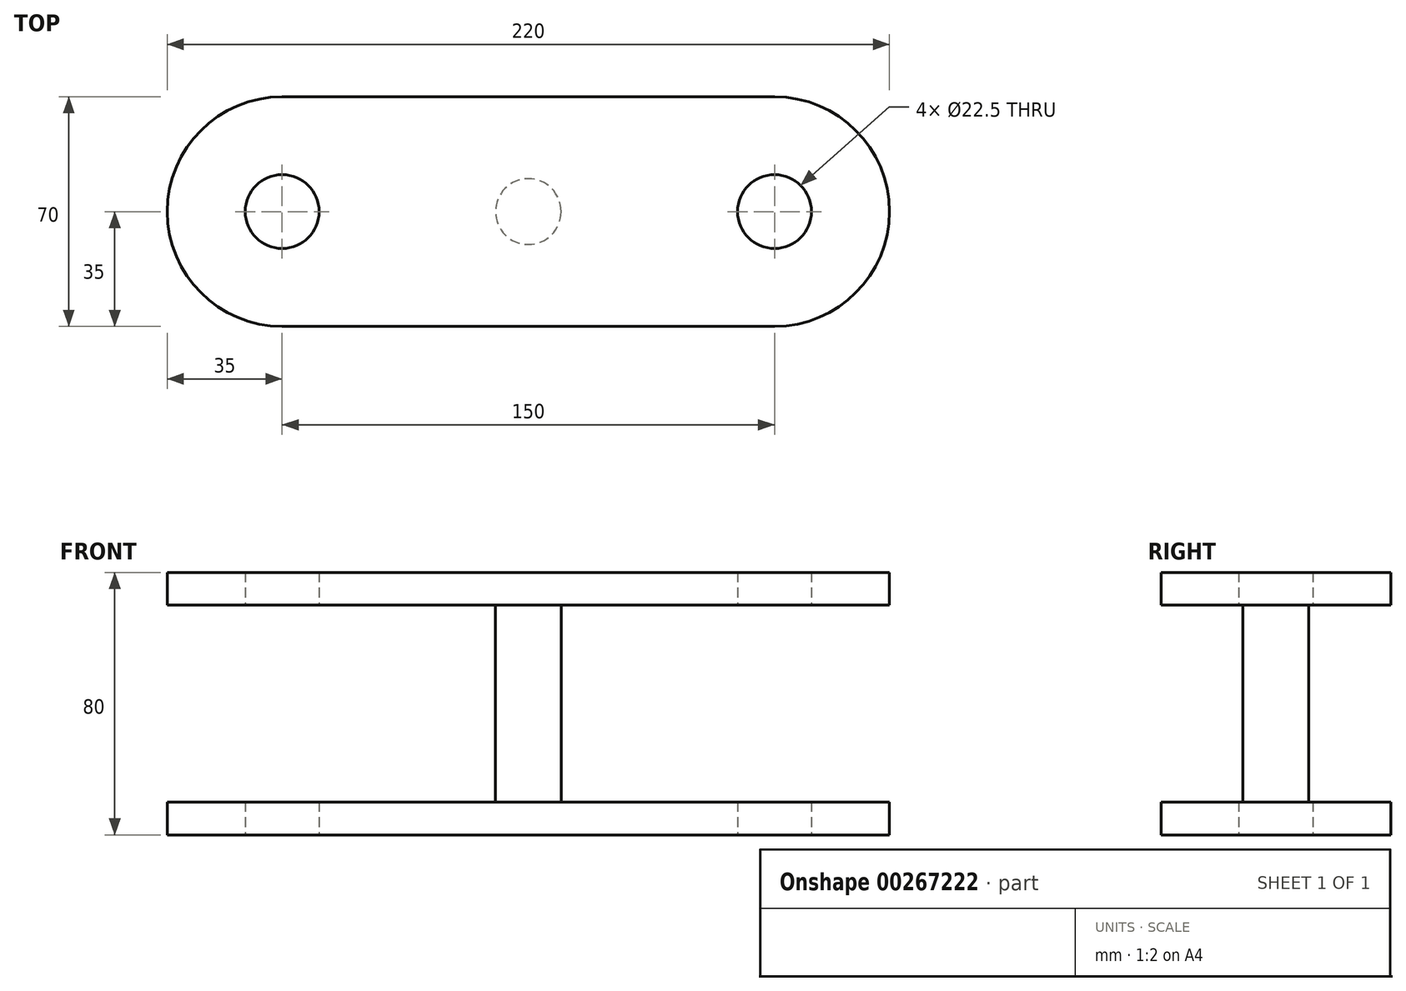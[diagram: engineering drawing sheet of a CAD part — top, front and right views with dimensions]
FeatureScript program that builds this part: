
annotation { "Feature Type Name" : "Feature", "Feature Type Description" : "" }
export const myFeature = defineFeature(function(context is Context, id is Id, definition is map)
    precondition{}
    {
        {
            var Q0;
            Q0=qCreatedBy(makeId("Top.planeOp"),FACE);
            var sketch = newSketch(context, id + "F0", { "sketchPlane" : qUnion([Q0])});
            skArc(sketch, "E0", {"start": v(-75, 35) * mm, "mid": v(-110, 0) * mm, "end": v(-75, -35) * mm});
            skArc(sketch, "E1", {"start": v(75, -35) * mm, "mid": v(110, 0) * mm, "end": v(75, 35) * mm});
            skLineSegment(sketch, "E2", {"start": v(-75, 35) * mm, "end": v(75, 35) * mm});
            skLineSegment(sketch, "E3", {"start": v(-75, -35) * mm, "end": v(75, -35) * mm});
            skArc(sketch, "E4", {"start": v(42.5, 0) * mm, "mid": v(75, -32.5) * mm, "end": v(107.5, 0) * mm});
            skArc(sketch, "E5", {"start": v(-107.5, 0) * mm, "mid": v(-75, -32.5) * mm, "end": v(-42.5, 0) * mm});
            skLineSegment(sketch, "E6", {"start": v(-42.5, 0) * mm, "end": v(-107.5, 0) * mm});
            skLineSegment(sketch, "E7", {"start": v(42.5, 0) * mm, "end": v(107.5, 0) * mm});
            skCircle(sketch, "E8", {"center": v(-75, 0) * mm, "radius": 11.25 * mm});
            skCircle(sketch, "E9", {"center": v(75, 0) * mm, "radius": 11.25 * mm});
            skCircle(sketch, "E10", {"center": v(0, 0) * mm, "radius": 10 * mm});
            skSolve(sketch);
        }
        {
            var Q0;
            {var subQ0=sQuery(id+"F0.wireOp",EDGE,"E5");Q0=makeQuery(id+"F0.imprint","IMPRINT",FACE,{"disambiguationData":[TD([[makeQuery(id+"F0.imprint","IMPRINT",EDGE,{"derivedFrom":subQ0}),1.0]])]});}
            var Q1;
            {var subQ0=sQuery(id+"F0.wireOp",EDGE,"E4");Q1=makeQuery(id+"F0.imprint","IMPRINT",FACE,{"disambiguationData":[TD([[makeQuery(id+"F0.imprint","IMPRINT",EDGE,{"derivedFrom":subQ0}),1.0]])]});}
            var Q2;
            Q2=makeQuery(id+"F0.imprint","IMPRINT",FACE,{"disambiguationData":[TD([[makeQuery(id+"F0.imprint","IMPRINT",EDGE,{"derivedFrom":sQuery(id+"F0.wireOp",EDGE,"E0")}),1.0]])]});
            var Q3;
            Q3=makeQuery(id+"F0.imprint","IMPRINT",FACE,{"disambiguationData":[TD([[makeQuery(id+"F0.imprint","IMPRINT",EDGE,{"derivedFrom":sQuery(id+"F0.wireOp",EDGE,"E10")}),1.0]])]});
            extrude(context, id + "F1", {"entities" : qUnion([Q0, Q1, Q2, Q3]), "endBound" : BoundingType.SYMMETRIC, "depth" : 80 * mm});
        }
        {
            var Q0;
            Q0=makeQuery(id+"F0.imprint","IMPRINT",FACE,{"disambiguationData":[TD([[makeQuery(id+"F0.imprint","IMPRINT",EDGE,{"derivedFrom":sQuery(id+"F0.wireOp",EDGE,"E5")}),1.0]])]});
            var Q1;
            Q1=makeQuery(id+"F0.imprint","IMPRINT",FACE,{"disambiguationData":[TD([[makeQuery(id+"F0.imprint","IMPRINT",EDGE,{"derivedFrom":sQuery(id+"F0.wireOp",EDGE,"E0")}),1.0]])]});
            var Q2;
            Q2=makeQuery(id+"F0.imprint","IMPRINT",FACE,{"disambiguationData":[TD([[makeQuery(id+"F0.imprint","IMPRINT",EDGE,{"derivedFrom":sQuery(id+"F0.wireOp",EDGE,"E4")}),1.0]])]});
            extrude(context, id + "F2", {"entities" : qUnion([Q0, Q1, Q2]), "operationType" : NewBodyOperationType.REMOVE, "endBound" : BoundingType.SYMMETRIC, "depth" : 60 * mm});
        }
    });
